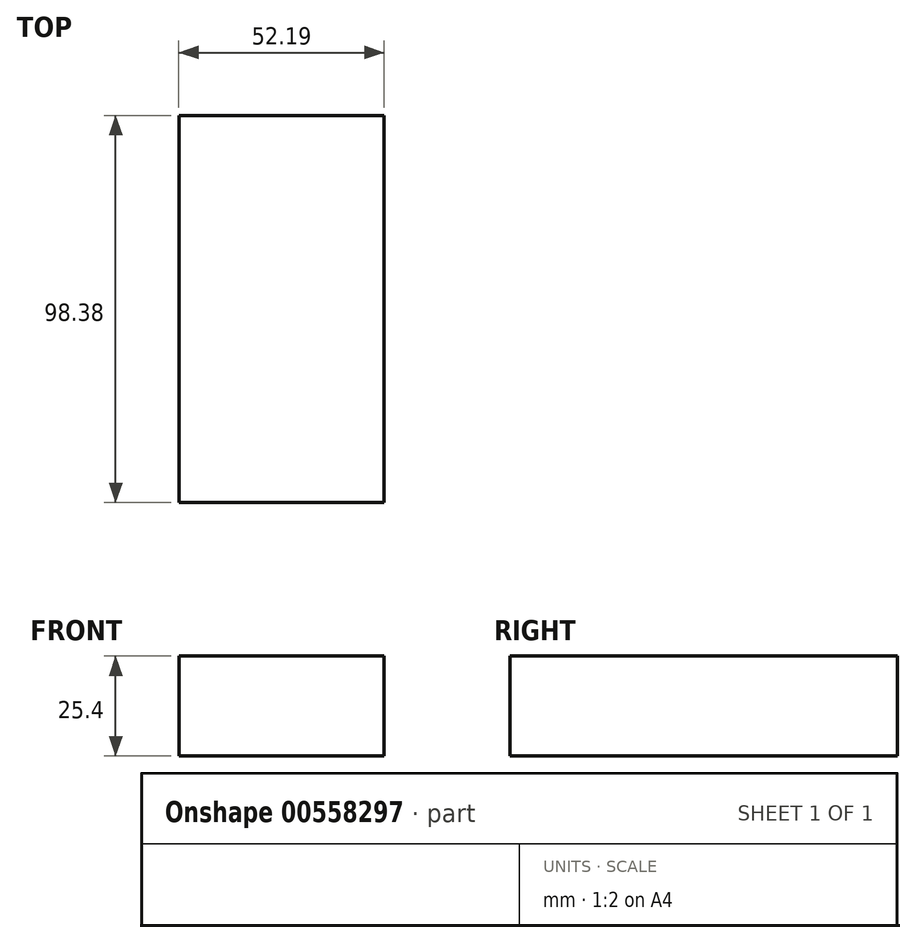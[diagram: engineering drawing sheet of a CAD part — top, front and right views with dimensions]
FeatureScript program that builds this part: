
annotation { "Feature Type Name" : "Feature", "Feature Type Description" : "" }
export const myFeature = defineFeature(function(context is Context, id is Id, definition is map)
    precondition{}
    {
        {
            var Q0;
            Q0=qCreatedBy(makeId("Top.planeOp"),FACE);
            var sketch = newSketch(context, id + "F0", { "sketchPlane" : qUnion([Q0])});
            skLineSegment(sketch, "E0.bottom", {"start": v(-25.78, -40.2) * mm, "end": v(26.4, -40.2) * mm});
            skLineSegment(sketch, "E0.top", {"start": v(-25.78, 58.18) * mm, "end": v(26.4, 58.18) * mm});
            skLineSegment(sketch, "E0.left", {"start": v(-25.78, -40.2) * mm, "end": v(-25.78, 58.18) * mm});
            skLineSegment(sketch, "E0.right", {"start": v(26.4, -40.2) * mm, "end": v(26.4, 58.18) * mm});
            skSolve(sketch);
        }
        {
            var Q0;
            Q0=makeQuery(id+"F0.imprint","IMPRINT",FACE,{"disambiguationData":[TD([[makeQuery(id+"F0.imprint","IMPRINT",EDGE,{"derivedFrom":sQuery(id+"F0.wireOp",EDGE,"E0.bottom")}),1.0]])]});
            extrude(context, id + "F1", {"entities" : qUnion([Q0]), "depth" : 25.4 * mm, "offsetDistance" : 25.4 * mm});
        }
    });
